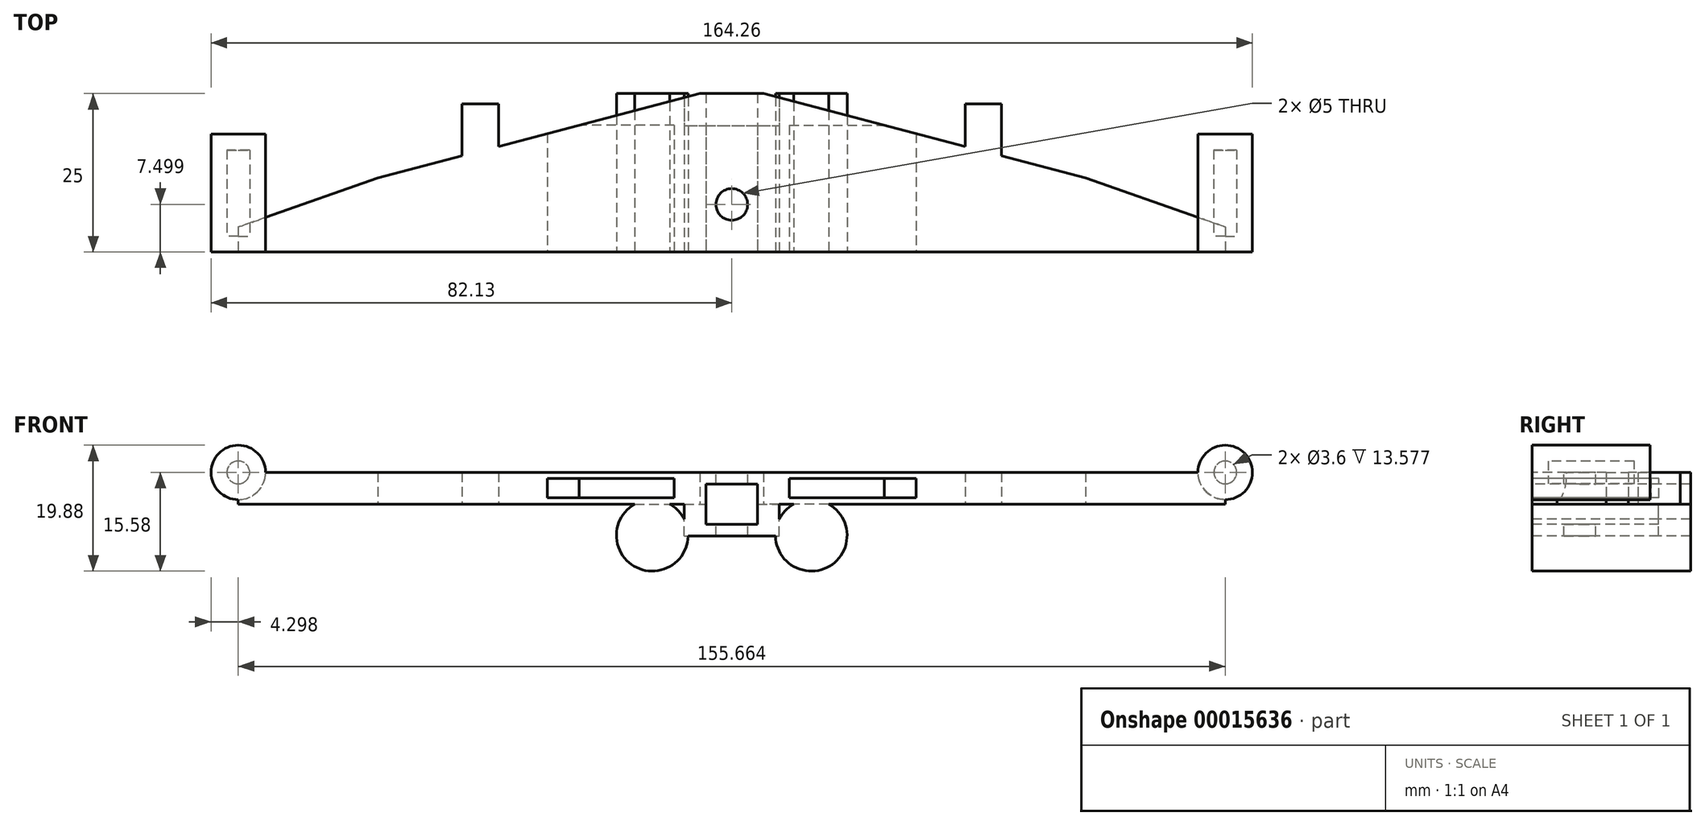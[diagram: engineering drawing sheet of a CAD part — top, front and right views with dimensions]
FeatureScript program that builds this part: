
annotation { "Feature Type Name" : "Feature", "Feature Type Description" : "" }
export const myFeature = defineFeature(function(context is Context, id is Id, definition is map)
    precondition{}
    {
        {
            var Q0;
            Q0=qCreatedBy(makeId("Top.planeOp"),FACE);
            var sketch = newSketch(context, id + "F0", { "sketchPlane" : qUnion([Q0])});
            skLineSegment(sketch, "E0.bottom", {"start": v(-5, 16.64) * mm, "end": v(5, 16.64) * mm});
            skLineSegment(sketch, "E0.top", {"start": v(-5, -8.36) * mm, "end": v(5, -8.36) * mm});
            skLineSegment(sketch, "E0.left", {"start": v(-5, 16.64) * mm, "end": v(-5, -8.36) * mm});
            skLineSegment(sketch, "E0.right", {"start": v(5, 16.64) * mm, "end": v(5, -8.36) * mm});
            skLineSegment(sketch, "E1", {"start": v(0, -8.36) * mm, "end": v(0, 26.19) * mm, "construction": true});
            skLineSegment(sketch, "E2", {"start": v(0, 26.19) * mm, "end": v(0, 27.94) * mm, "construction": true});
            skLineSegment(sketch, "E3.MirrorCS", {"start": v(5, -8.36) * mm, "end": v(55.8, -8.36) * mm});
            skLineSegment(sketch, "E4.MirrorCS", {"start": v(55.8, 3.31) * mm, "end": v(5, 16.64) * mm});
            skLineSegment(sketch, "E5", {"start": v(55.8, 3.31) * mm, "end": v(77.83, -4.42) * mm});
            skLineSegment(sketch, "E6", {"start": v(77.83, -4.42) * mm, "end": v(77.83, -8.36) * mm});
            skPoint(sketch, "E7.MirrorCS.start.orphan", {"position": v(55.8, -8.36) * mm});
            skLineSegment(sketch, "E8", {"start": v(55.8, -8.36) * mm, "end": v(77.83, -8.36) * mm});
            skLineSegment(sketch, "E9.MirrorCS", {"start": v(-55.8, 3.31) * mm, "end": v(-5, 16.64) * mm});
            skLineSegment(sketch, "E10.MirrorCS", {"start": v(-5, -8.36) * mm, "end": v(-55.8, -8.36) * mm});
            skLineSegment(sketch, "E11.MirrorCS", {"start": v(-55.8, 3.31) * mm, "end": v(-77.83, -4.42) * mm});
            skLineSegment(sketch, "E12.MirrorCS", {"start": v(-55.8, -8.36) * mm, "end": v(-77.83, -8.36) * mm});
            skLineSegment(sketch, "E13.MirrorCS", {"start": v(-77.83, -4.42) * mm, "end": v(-77.83, -8.36) * mm});
            skLineSegment(sketch, "E14", {"start": v(77.83, -4.42) * mm, "end": v(77.83, 0) * mm});
            skLineSegment(sketch, "E15", {"start": v(77.83, 0) * mm, "end": v(80.33, 0) * mm});
            skLineSegment(sketch, "E16", {"start": v(80.33, 0) * mm, "end": v(80.33, -8.3) * mm});
            skLineSegment(sketch, "E17", {"start": v(80.33, -8.3) * mm, "end": v(77.83, -8.36) * mm});
            skLineSegment(sketch, "E18", {"start": v(78.52, 3.86) * mm, "end": v(78.52, 3.87) * mm});
            skLineSegment(sketch, "E19.MirrorCS", {"start": v(-78.52, 3.86) * mm, "end": v(-78.52, 3.87) * mm});
            skPoint(sketch, "E20.orphan", {"position": v(-77.83, 0) * mm});
            skPoint(sketch, "E21.orphan", {"position": v(-80.33, 0) * mm});
            skPoint(sketch, "E22.MirrorCS.start.orphan", {"position": v(-77.83, -8.36) * mm});
            skPoint(sketch, "E23.MirrorCS.start.orphan", {"position": v(-77.83, -4.42) * mm});
            skLineSegment(sketch, "E24.MirrorCS", {"start": v(-77.83, -4.42) * mm, "end": v(-77.83, 0) * mm});
            skLineSegment(sketch, "E25.MirrorCS", {"start": v(-77.83, 0) * mm, "end": v(-80.33, 0) * mm});
            skLineSegment(sketch, "E26.MirrorCS", {"start": v(-80.33, 0) * mm, "end": v(-80.33, -8.3) * mm});
            skLineSegment(sketch, "E27.MirrorCS", {"start": v(-80.33, -8.3) * mm, "end": v(-77.83, -8.36) * mm});
            skLineSegment(sketch, "E28", {"start": v(-36.8, 8.3) * mm, "end": v(-36.8, 15.01) * mm});
            skLineSegment(sketch, "E29", {"start": v(-36.8, 15.01) * mm, "end": v(-42.53, 15.01) * mm});
            skLineSegment(sketch, "E30", {"start": v(-42.53, 15.01) * mm, "end": v(-42.53, 6.8) * mm});
            skLineSegment(sketch, "E31.MirrorCS", {"start": v(42.53, 15.01) * mm, "end": v(42.53, 6.8) * mm});
            skLineSegment(sketch, "E32.MirrorCS", {"start": v(36.8, 8.3) * mm, "end": v(36.8, 15.01) * mm});
            skLineSegment(sketch, "E33.MirrorCS", {"start": v(36.8, 15.01) * mm, "end": v(42.53, 15.01) * mm});
            skLineSegment(sketch, "E34", {"start": v(-77.83, -8.36) * mm, "end": v(-5, -8.36) * mm});
            skLineSegment(sketch, "E35", {"start": v(5, -8.36) * mm, "end": v(77.83, -8.36) * mm});
            skSolve(sketch);
        }
        {
            var Q0;
            {var subQ5=sQuery(id+"F0.wireOp",EDGE,"E0.right");Q0=makeQuery(id+"F0.imprint","IMPRINT",FACE,{"disambiguationData":[TD([[makeQuery(id+"F0.imprint","IMPRINT",EDGE,{"derivedFrom":subQ5}),1.0]])]});}
            var Q1;
            {var subQ7=sQuery(id+"F0.wireOp",EDGE,"E0.left");Q1=makeQuery(id+"F0.imprint","IMPRINT",FACE,{"disambiguationData":[TD([[makeQuery(id+"F0.imprint","IMPRINT",EDGE,{"derivedFrom":subQ7}),-1.0]])]});}
            var Q2;
            Q2=makeQuery(id+"F0.imprint","IMPRINT",FACE,{"disambiguationData":[TD([[makeQuery(id+"F0.imprint","IMPRINT",EDGE,{"derivedFrom":sQuery(id+"F0.wireOp",EDGE,"E0.bottom")}),-1.0]])]});
            var Q3;
            {var subQ1=sQuery(id+"F0.wireOp",EDGE,"E28");Q3=makeQuery(id+"F0.imprint","IMPRINT",FACE,{"disambiguationData":[TD([[makeQuery(id+"F0.imprint","IMPRINT",EDGE,{"derivedFrom":subQ1}),1.0]])]});}
            var Q4;
            {var subQ1=sQuery(id+"F0.wireOp",EDGE,"E31.MirrorCS");Q4=makeQuery(id+"F0.imprint","IMPRINT",FACE,{"disambiguationData":[TD([[makeQuery(id+"F0.imprint","IMPRINT",EDGE,{"derivedFrom":subQ1}),-1.0]])]});}
            extrude(context, id + "F1", {"entities" : qUnion([Q0, Q1, Q2, Q3, Q4]), "depth" : 5 * mm});
        }
        {
            var Q0;
            Q0=makeQuery(id+"F1.opExtrude","SWEPT_FACE",FACE,{"disambiguationData":[OSD([sQuery(id+"F0.wireOp",EDGE,"E0.top"),sQuery(id+"F0.wireOp",EDGE,"e8cc36b1-fd7a-433f-b142-e09a31d02a13"),sQuery(id+"F0.wireOp",EDGE,"ddf1b872-187a-419e-aba2-32dc34e63613.bottom"),sQuery(id+"F0.wireOp",EDGE,"E3.MirrorCS"),sQuery(id+"F0.wireOp",EDGE,"50d09c58-4173-4b4d-8a5c-3e18dbf53120")])]});
            var sketch = newSketch(context, id + "F2", { "sketchPlane" : qUnion([Q0])});
            skLineSegment(sketch, "E36.rect.bottom", {"start": v(-4.07, -3.17) * mm, "end": v(4.07, -3.17) * mm});
            skLineSegment(sketch, "E36.rect.top", {"start": v(-4.07, 3.16) * mm, "end": v(4.07, 3.16) * mm});
            skLineSegment(sketch, "E36.rect.left", {"start": v(-4.07, -3.17) * mm, "end": v(-4.07, 3.16) * mm});
            skLineSegment(sketch, "E36.rect.right", {"start": v(4.07, -3.17) * mm, "end": v(4.07, 3.16) * mm});
            skPoint(sketch, "E36.rect.middle", {"position": v(0, 0) * mm});
            skLineSegment(sketch, "E37.rect.bottom", {"start": v(-7.5, -5.02) * mm, "end": v(7.5, -5.02) * mm});
            skLineSegment(sketch, "E37.rect.top", {"start": v(-7.5, 5.02) * mm, "end": v(7.5, 5.02) * mm});
            skLineSegment(sketch, "E37.rect.left", {"start": v(-7.5, -5.02) * mm, "end": v(-7.5, 5.02) * mm});
            skLineSegment(sketch, "E37.rect.right", {"start": v(7.5, -5.02) * mm, "end": v(7.5, 5.02) * mm});
            skSolve(sketch);
        }
        {
            var Q0;
            {var subQ10=sQuery(id+"F2.wireOp",EDGE,"E36.rect.bottom");Q0=makeQuery(id+"F2.imprint","IMPRINT",FACE,{"disambiguationData":[TD([[makeQuery(id+"F2.imprint","IMPRINT",EDGE,{"derivedFrom":subQ10}),-1.0]])]});}
            extrude(context, id + "F3", {"entities" : qUnion([Q0]), "operationType" : NewBodyOperationType.ADD, "oppositeDirection" : true, "depth" : 19.93 * mm});
        }
        {
            var Q0;
            {var subQ3=sQuery(id+"F2.wireOp",EDGE,"E36.rect.top");Q0=makeQuery(id+"F2.imprint","IMPRINT",FACE,{"disambiguationData":[TD([[makeQuery(id+"F2.imprint","IMPRINT",EDGE,{"derivedFrom":subQ3}),-1.0]])]});}
            extrude(context, id + "F4", {"entities" : qUnion([Q0]), "operationType" : NewBodyOperationType.REMOVE, "oppositeDirection" : true, "depth" : 25 * mm});
        }
        {
            var Q0;
            Q0=makeQuery(id+"F1.opExtrude","CAP_FACE",FACE,{"disambiguationData":[OSD([sQuery(id+"F0.wireOp",EDGE,"E0.bottom"),sQuery(id+"F0.wireOp",EDGE,"E0.top"),sQuery(id+"F0.wireOp",EDGE,"e8cc36b1-fd7a-433f-b142-e09a31d02a13"),sQuery(id+"F0.wireOp",EDGE,"63a4df71-0616-4f30-9dd8-0f9538299a92"),sQuery(id+"F0.wireOp",EDGE,"ddf1b872-187a-419e-aba2-32dc34e63613.bottom"),sQuery(id+"F0.wireOp",EDGE,"ddf1b872-187a-419e-aba2-32dc34e63613.left"),sQuery(id+"F0.wireOp",EDGE,"e8699522-5a5a-421a-af3f-ac40b27ec4fe.bottom"),sQuery(id+"F0.wireOp",EDGE,"e8699522-5a5a-421a-af3f-ac40b27ec4fe.top"),sQuery(id+"F0.wireOp",EDGE,"e8699522-5a5a-421a-af3f-ac40b27ec4fe.right"),sQuery(id+"F0.wireOp",EDGE,"E3.MirrorCS"),sQuery(id+"F0.wireOp",EDGE,"E4.MirrorCS"),sQuery(id+"F0.wireOp",EDGE,"87cc3f43-4a3a-4b3d-b893-0e91a26680800.MirrorCS"),sQuery(id+"F0.wireOp",EDGE,"3fc1773d-df33-402e-a4e6-f0911ea45a1a0.MirrorCS"),sQuery(id+"F0.wireOp",EDGE,"e6077c88-c3b5-436c-8a9f-b22728a443b80.MirrorCS"),sQuery(id+"F0.wireOp",EDGE,"bc56a379-6f47-48b1-a7f0-b0f788b93a670.MirrorCS")])],"isStart":false});
            var sketch = newSketch(context, id + "F5", { "sketchPlane" : qUnion([Q0])});
            skPoint(sketch, "E38.center.orphan", {"position": v(0, 0) * mm});
            skCircle(sketch, "E39", {"center": v(0, -0.86) * mm, "radius": 2.5 * mm});
            skSolve(sketch);
        }
        {
            var Q0;
            Q0=makeQuery(id+"F5.imprint","IMPRINT",FACE,{"disambiguationData":[TD([[makeQuery(id+"F5.imprint","IMPRINT",EDGE,{"derivedFrom":sQuery(id+"F5.wireOp",EDGE,"E39")}),1.0]])]});
            extrude(context, id + "F6", {"entities" : qUnion([Q0]), "operationType" : NewBodyOperationType.REMOVE, "oppositeDirection" : true, "depth" : 25 * mm});
        }
        {
            var Q0;
            {var subQ0=sQuery(id+"F0.wireOp",EDGE,"E0.top");var subQ1=sQuery(id+"F0.wireOp",EDGE,"e8cc36b1-fd7a-433f-b142-e09a31d02a13");var subQ2=sQuery(id+"F0.wireOp",EDGE,"ddf1b872-187a-419e-aba2-32dc34e63613.bottom");var subQ3=sQuery(id+"F0.wireOp",EDGE,"E3.MirrorCS");Q0=makeQuery(id+"F3.boolean.opBoolean","MERGE",FACE,{"derivedFrom":[makeQuery(id+"F1.opExtrude","SWEPT_FACE",FACE,{"disambiguationData":[OSD([subQ0,subQ1,subQ2,subQ3])]}),makeQuery(id+"F3.opExtrude","CAP_FACE",FACE,{"disambiguationData":[OSD([subQ0,subQ1,subQ2,subQ3,sQuery(id+"F2.wireOp",EDGE,"E36.rect.bottom"),sQuery(id+"F2.wireOp",EDGE,"E36.rect.left"),sQuery(id+"F2.wireOp",EDGE,"E36.rect.right"),sQuery(id+"F2.wireOp",EDGE,"E37.rect.bottom"),sQuery(id+"F2.wireOp",EDGE,"E37.rect.left"),sQuery(id+"F2.wireOp",EDGE,"E37.rect.right")])],"isStart":true})]});}
            var sketch = newSketch(context, id + "F7", { "sketchPlane" : qUnion([Q0])});
            skLineSegment(sketch, "E40", {"start": v(0, 64.46) * mm, "end": v(0, -67.62) * mm, "construction": true});
            skLineSegment(sketch, "E41.bottom", {"start": v(-9.07, 1) * mm, "end": v(-29.07, 1) * mm});
            skLineSegment(sketch, "E41.top", {"start": v(-9.07, 4.05) * mm, "end": v(-29.07, 4.05) * mm});
            skLineSegment(sketch, "E41.left", {"start": v(-9.07, 1) * mm, "end": v(-9.07, 4.05) * mm});
            skLineSegment(sketch, "E41.right", {"start": v(-29.07, 1) * mm, "end": v(-29.07, 4.05) * mm});
            skLineSegment(sketch, "E42.MirrorCS", {"start": v(9.07, 4.05) * mm, "end": v(29.07, 4.05) * mm});
            skLineSegment(sketch, "E43.MirrorCS", {"start": v(9.07, 1) * mm, "end": v(29.07, 1) * mm});
            skLineSegment(sketch, "E44", {"start": v(9.07, 4.05) * mm, "end": v(9.07, 1) * mm});
            skLineSegment(sketch, "E45", {"start": v(29.07, 4.05) * mm, "end": v(29.07, 1) * mm});
            skSolve(sketch);
        }
        {
            var Q0;
            Q0=makeQuery(id+"F7.imprint","IMPRINT",FACE,{"disambiguationData":[TD([[makeQuery(id+"F7.imprint","IMPRINT",EDGE,{"derivedFrom":sQuery(id+"F7.wireOp",EDGE,"E41.bottom")}),-1.0]])]});
            extrude(context, id + "F8", {"entities" : qUnion([Q0]), "operationType" : NewBodyOperationType.REMOVE, "oppositeDirection" : true, "depth" : 20 * mm});
        }
        {
            var Q0;
            Q0=makeQuery(id+"F7.imprint","IMPRINT",FACE,{"disambiguationData":[TD([[makeQuery(id+"F7.imprint","IMPRINT",EDGE,{"derivedFrom":sQuery(id+"F7.wireOp",EDGE,"E42.MirrorCS")}),-1.0]])]});
            extrude(context, id + "F9", {"entities" : qUnion([Q0]), "operationType" : NewBodyOperationType.REMOVE, "oppositeDirection" : true, "depth" : 20 * mm});
        }
        {
            var Q0;
            Q0=makeQuery(id+"F7.imprint","IMPRINT",FACE,{"disambiguationData":[TD([[makeQuery(id+"F7.imprint","IMPRINT",EDGE,{"derivedFrom":sQuery(id+"F7.wireOp",EDGE,"E41.bottom")}),1.0]])]});
            var sketch = newSketch(context, id + "F10", { "sketchPlane" : qUnion([Q0])});
            skCircle(sketch, "E46", {"center": v(-12.54, -4.93) * mm, "radius": 5.65 * mm});
            skCircle(sketch, "E47.MirrorC", {"center": v(12.54, -4.93) * mm, "radius": 5.65 * mm});
            skSolve(sketch);
        }
        {
            var Q0;
            {var subQ3=sQuery(id+"F2.wireOp",EDGE,"E37.rect.right");var subQ4=sQuery(id+"F2.wireOp",EDGE,"E37.rect.bottom");var subQ10=makeQuery(id+"F7.imprint","IMPRINT",EDGE,{"derivedFrom":makeQuery(id+"F3.opExtrude","CAP_EDGE",EDGE,{"disambiguationData":[OSD([subQ3])],"isStart":true})});var subQ12=makeQuery(id+"F7.imprint","IMPRINT",EDGE,{"derivedFrom":makeQuery(id+"F3.opExtrude","CAP_EDGE",EDGE,{"disambiguationData":[OSD([subQ4])],"isStart":true})});var subQ13=makeQuery(id+"F10.imprint","INTERSECT",VERTEX,{"derivedFrom":[subQ12,subQ10]});Q0=makeQuery(id+"F10.imprint","IMPRINT",FACE,{"disambiguationData":[TD([[makeQuery(id+"F10.imprint","IMPRINT",EDGE,{"disambiguationData":[TD([[subQ13,1.0]])],"derivedFrom":subQ12}),-1.0]])]});}
            var Q1;
            {var subQ3=sQuery(id+"F2.wireOp",EDGE,"E37.rect.bottom");var subQ4=sQuery(id+"F2.wireOp",EDGE,"E37.rect.left");var subQ10=makeQuery(id+"F7.imprint","IMPRINT",EDGE,{"derivedFrom":makeQuery(id+"F3.opExtrude","CAP_EDGE",EDGE,{"disambiguationData":[OSD([subQ4])],"isStart":true})});var subQ12=makeQuery(id+"F7.imprint","IMPRINT",EDGE,{"derivedFrom":makeQuery(id+"F3.opExtrude","CAP_EDGE",EDGE,{"disambiguationData":[OSD([subQ3])],"isStart":true})});var subQ13=makeQuery(id+"F10.imprint","INTERSECT",VERTEX,{"derivedFrom":[subQ12,subQ10]});Q1=makeQuery(id+"F10.imprint","IMPRINT",FACE,{"disambiguationData":[TD([[makeQuery(id+"F10.imprint","IMPRINT",EDGE,{"disambiguationData":[TD([[subQ13,-1.0]])],"derivedFrom":subQ12}),-1.0]])]});}
            extrude(context, id + "F11", {"entities" : qUnion([Q0, Q1]), "operationType" : NewBodyOperationType.ADD, "oppositeDirection" : true, "depth" : 25 * mm});
        }
        {
            var Q0;
            Q0=makeQuery(id+"F1.opExtrude","CAP_FACE",FACE,{"disambiguationData":[OSD([sQuery(id+"F0.wireOp",EDGE,"E0.bottom"),sQuery(id+"F0.wireOp",EDGE,"E0.top"),sQuery(id+"F0.wireOp",EDGE,"E4.MirrorCS"),sQuery(id+"F0.wireOp",EDGE,"E5"),sQuery(id+"F0.wireOp",EDGE,"E6"),sQuery(id+"F0.wireOp",EDGE,"E9.MirrorCS"),sQuery(id+"F0.wireOp",EDGE,"E11.MirrorCS"),sQuery(id+"F0.wireOp",EDGE,"E13.MirrorCS"),sQuery(id+"F0.wireOp",EDGE,"E28"),sQuery(id+"F0.wireOp",EDGE,"E29"),sQuery(id+"F0.wireOp",EDGE,"E30"),sQuery(id+"F0.wireOp",EDGE,"E31.MirrorCS"),sQuery(id+"F0.wireOp",EDGE,"E32.MirrorCS"),sQuery(id+"F0.wireOp",EDGE,"E33.MirrorCS"),sQuery(id+"F0.wireOp",EDGE,"E34"),sQuery(id+"F0.wireOp",EDGE,"E35")])],"isStart":false});
            var sketch = newSketch(context, id + "F12", { "sketchPlane" : qUnion([Q0])});
            skLineSegment(sketch, "E48", {"start": v(0, -0.86) * mm, "end": v(0, 57.25) * mm, "construction": true});
            skLineSegment(sketch, "E49", {"start": v(0, 57.25) * mm, "end": v(0, -45.7) * mm, "construction": true});
            skLineSegment(sketch, "E50.bottom", {"start": v(-77.83, -8.36) * mm, "end": v(-73.53, -8.36) * mm});
            skLineSegment(sketch, "E50.top", {"start": v(-77.83, 10.22) * mm, "end": v(-73.53, 10.22) * mm});
            skLineSegment(sketch, "E50.left", {"start": v(-77.83, -8.36) * mm, "end": v(-77.83, 10.22) * mm});
            skLineSegment(sketch, "E50.right", {"start": v(-73.53, -8.36) * mm, "end": v(-73.53, 10.22) * mm});
            skLineSegment(sketch, "E51.MirrorCS", {"start": v(73.53, -8.36) * mm, "end": v(73.53, 10.22) * mm});
            skLineSegment(sketch, "E52.MirrorCS", {"start": v(77.83, -8.36) * mm, "end": v(77.83, 10.22) * mm});
            skLineSegment(sketch, "E53.MirrorCS", {"start": v(77.83, 10.22) * mm, "end": v(73.53, 10.22) * mm});
            skLineSegment(sketch, "E54.MirrorCS", {"start": v(77.83, -8.36) * mm, "end": v(73.53, -8.36) * mm});
            skSolve(sketch);
        }
        {
            var Q0;
            {var subQ3=sQuery(id+"F12.wireOp",EDGE,"E50.top");Q0=makeQuery(id+"F12.imprint","IMPRINT",FACE,{"disambiguationData":[TD([[makeQuery(id+"F12.imprint","IMPRINT",EDGE,{"derivedFrom":subQ3}),-1.0]])]});}
            var Q1;
            {var subQ5=sQuery(id+"F12.wireOp",EDGE,"E50.bottom");Q1=makeQuery(id+"F12.imprint","IMPRINT",FACE,{"disambiguationData":[TD([[makeQuery(id+"F12.imprint","IMPRINT",EDGE,{"derivedFrom":subQ5}),1.0]])]});}
            var Q2;
            Q2=sQuery(id+"F12.wireOp",EDGE,"E50.left");
            revolve(context, id + "F13", {"operationType" : NewBodyOperationType.ADD, "entities" : qUnion([Q0, Q1]), "axis" : qUnion([Q2]), "revolveType" : RevolveType.FULL});
        }
        {
            var Q0;
            {var subQ5=sQuery(id+"F12.wireOp",EDGE,"E53.MirrorCS");Q0=makeQuery(id+"F12.imprint","IMPRINT",FACE,{"disambiguationData":[TD([[makeQuery(id+"F12.imprint","IMPRINT",EDGE,{"derivedFrom":subQ5}),1.0]])]});}
            var Q1;
            {var subQ5=sQuery(id+"F12.wireOp",EDGE,"E54.MirrorCS");Q1=makeQuery(id+"F12.imprint","IMPRINT",FACE,{"disambiguationData":[TD([[makeQuery(id+"F12.imprint","IMPRINT",EDGE,{"derivedFrom":subQ5}),1.0]])]});}
            var Q2;
            Q2=sQuery(id+"F12.wireOp",EDGE,"E52.MirrorCS");
            revolve(context, id + "F14", {"operationType" : NewBodyOperationType.ADD, "entities" : qUnion([Q0, Q1]), "axis" : qUnion([Q2]), "revolveType" : RevolveType.FULL});
        }
        {
            var Q0;
            Q0=makeQuery(id+"F11.opExtrude","CAP_FACE",FACE,{"disambiguationData":[OSD([sQuery(id+"F0.wireOp",EDGE,"E0.top"),sQuery(id+"F0.wireOp",EDGE,"E34"),sQuery(id+"F0.wireOp",EDGE,"E35"),sQuery(id+"F2.wireOp",EDGE,"E37.rect.bottom"),sQuery(id+"F2.wireOp",EDGE,"E37.rect.right"),sQuery(id+"F10.wireOp",EDGE,"E47.MirrorC")])],"isStart":false});
            shell(context, id + "F15", {"entities" : qUnion([Q0]), "thickness" : 2.5 * mm});
        }
    });
